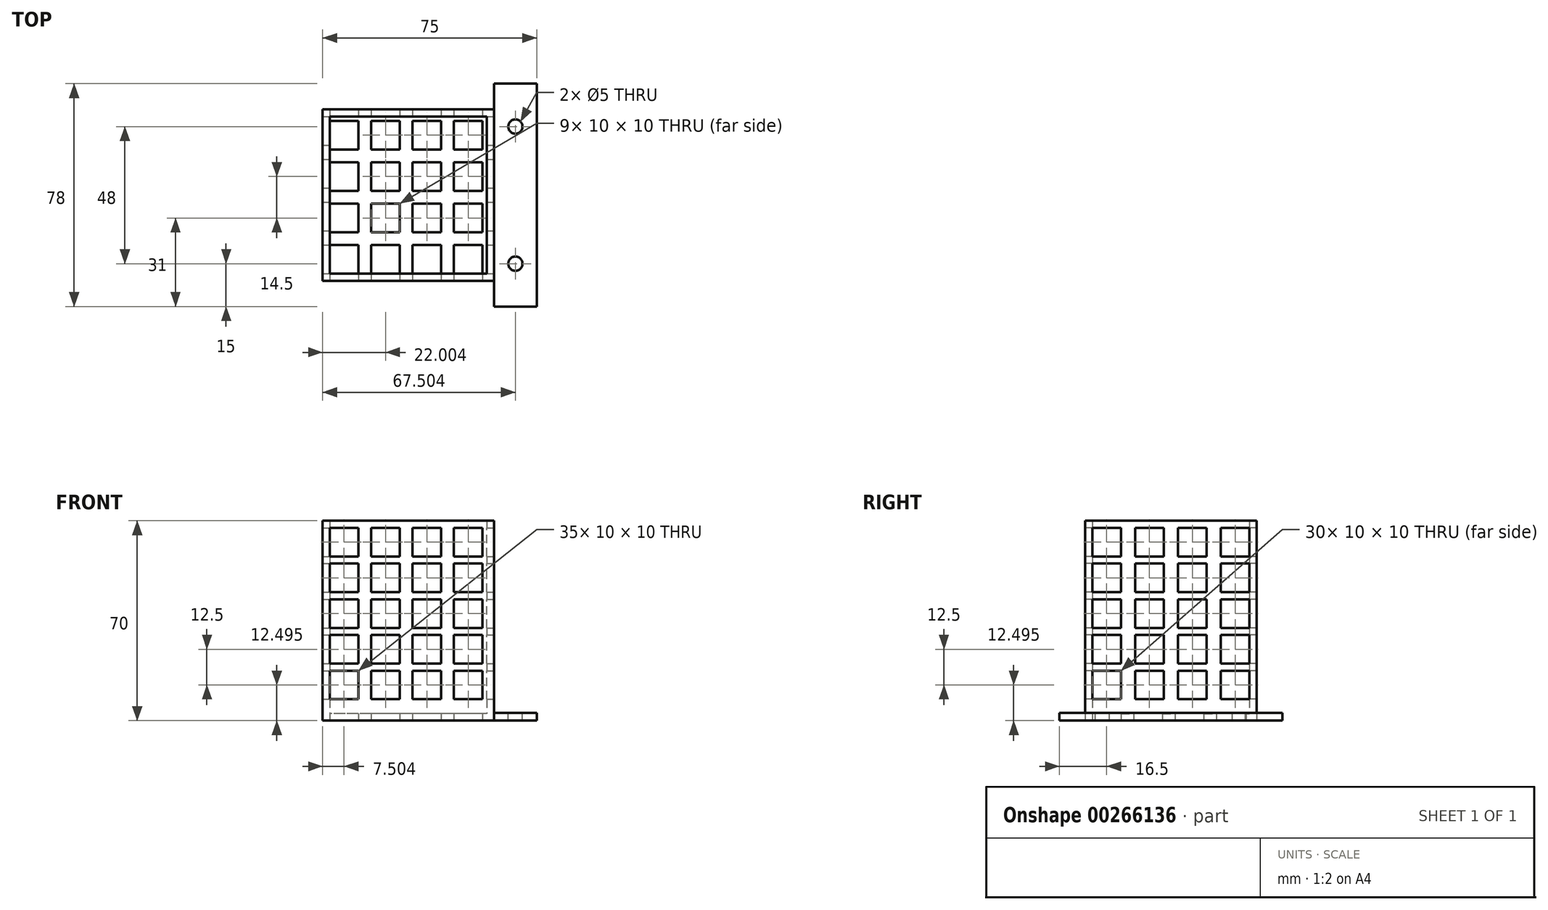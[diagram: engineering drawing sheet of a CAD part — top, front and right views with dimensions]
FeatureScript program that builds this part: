
annotation { "Feature Type Name" : "Feature", "Feature Type Description" : "" }
export const myFeature = defineFeature(function(context is Context, id is Id, definition is map)
    precondition{}
    {
        {
            var Q0;
            Q0=qCreatedBy(makeId("Front.planeOp"),FACE);
            var sketch = newSketch(context, id + "F0", { "sketchPlane" : qUnion([Q0])});
            skLineSegment(sketch, "E0", {"start": v(33.02, 18.38) * mm, "end": v(48.02, 18.38) * mm});
            skLineSegment(sketch, "E1", {"start": v(48.02, 18.38) * mm, "end": v(48.02, 21.13) * mm});
            skLineSegment(sketch, "E2", {"start": v(48.02, 21.13) * mm, "end": v(33.02, 21.13) * mm});
            skLineSegment(sketch, "E3", {"start": v(33.02, 21.13) * mm, "end": v(33.02, 18.38) * mm});
            skSolve(sketch);
        }
        {
            var Q0;
            Q0=qSketchRegion(id+"F0",true);
            extrude(context, id + "F1", {"entities" : qUnion([Q0]), "endBound" : BoundingType.SYMMETRIC, "depth" : 78 * mm});
        }
        {
            var Q0;
            Q0=makeQuery(id+"F1.opExtrude","SWEPT_FACE",FACE,{"disambiguationData":[OSD([sQuery(id+"F0.wireOp",EDGE,"E2")])]});
            var sketch = newSketch(context, id + "F2", { "sketchPlane" : qUnion([Q0])});
            skCircle(sketch, "E4", {"center": v(40.52, -24) * mm, "radius": 2.5 * mm});
            skCircle(sketch, "E5.0.1.0", {"center": v(40.52, 24) * mm, "radius": 2.5 * mm});
            skLineSegment(sketch, "E5.direction1", {"start": v(40.52, -24) * mm, "end": v(64.68, -24) * mm, "construction": true});
            skLineSegment(sketch, "E5.direction2", {"start": v(40.52, -24) * mm, "end": v(40.52, 24) * mm, "construction": true});
            skLineSegment(sketch, "E6.0", {"start": v(33.02, -39) * mm, "end": v(33.02, 39) * mm});
            skLineSegment(sketch, "E7.0", {"start": v(48.02, -39) * mm, "end": v(48.02, 39) * mm});
            skLineSegment(sketch, "E8", {"start": v(33.02, -1.08) * mm, "end": v(48.02, -1.08) * mm, "construction": true});
            skPoint(sketch, "E8.endSnap0", {"position": v(48.02, 0) * mm});
            skPoint(sketch, "E9", {"position": v(40.52, -1.08) * mm});
            skSolve(sketch);
        }
        {
            var Q0;
            Q0=makeQuery(id+"F2.imprint","IMPRINT",FACE,{"disambiguationData":[TD([[makeQuery(id+"F2.imprint","IMPRINT",EDGE,{"derivedFrom":sQuery(id+"F2.wireOp",EDGE,"E5.0.1.0")}),1.0]])]});
            var Q1;
            Q1=makeQuery(id+"F2.imprint","IMPRINT",FACE,{"disambiguationData":[TD([[makeQuery(id+"F2.imprint","IMPRINT",EDGE,{"derivedFrom":sQuery(id+"F2.wireOp",EDGE,"E4")}),1.0]])]});
            extrude(context, id + "F3", {"entities" : qUnion([Q0, Q1]), "operationType" : NewBodyOperationType.REMOVE, "endBound" : BoundingType.THROUGH_ALL, "oppositeDirection" : true, "depth" : 25 * mm});
        }
        {
            var Q0;
            Q0=makeQuery(id+"F1.opExtrude","SWEPT_FACE",FACE,{"disambiguationData":[OSD([sQuery(id+"F0.wireOp",EDGE,"E0")])]});
            var sketch = newSketch(context, id + "F4", { "sketchPlane" : qUnion([Q0])});
            skLineSegment(sketch, "E10", {"start": v(33.02, 30) * mm, "end": v(-26.98, 30) * mm});
            skLineSegment(sketch, "E11", {"start": v(33.02, -30) * mm, "end": v(-26.98, -30) * mm});
            skLineSegment(sketch, "E12", {"start": v(-26.98, 30) * mm, "end": v(-26.98, -30) * mm});
            skSolve(sketch);
        }
        {
            var Q0;
            {var subQ0=sQuery(id+"F4.wireOp",EDGE,"E10");Q0=makeQuery(id+"F4.imprint","IMPRINT",FACE,{"disambiguationData":[TD([[makeQuery(id+"F4.imprint","IMPRINT",EDGE,{"derivedFrom":subQ0}),1.0]])]});}
            extrude(context, id + "F5", {"entities" : qUnion([Q0]), "operationType" : NewBodyOperationType.ADD, "oppositeDirection" : true, "depth" : 70 * mm});
        }
        {
            var Q0;
            Q0=makeQuery(id+"F5.opExtrude","CAP_FACE",FACE,{"disambiguationData":[OSD([sQuery(id+"F0.wireOp",EDGE,"E0"),sQuery(id+"F0.wireOp",EDGE,"E3"),sQuery(id+"F4.wireOp",EDGE,"E10"),sQuery(id+"F4.wireOp",EDGE,"E11"),sQuery(id+"F4.wireOp",EDGE,"XroIyZZh-nZdX-ji37-o0S8-ZtPrHTp5OUbo")])],"isStart":false});
            shell(context, id + "F6", {"entities" : qUnion([Q0]), "thickness" : 2.5 * mm});
        }
        {
            var Q0;
            Q0=makeQuery(id+"F5.opExtrude","SWEPT_FACE",FACE,{"disambiguationData":[OSD([sQuery(id+"F0.wireOp",EDGE,"E0"),sQuery(id+"F0.wireOp",EDGE,"E3")])]});
            var sketch = newSketch(context, id + "F7", { "sketchPlane" : qUnion([Q0])});
            skLineSegment(sketch, "E13.bottom", {"start": v(-27.5, 85.88) * mm, "end": v(-17.5, 85.88) * mm});
            skLineSegment(sketch, "E13.top", {"start": v(-27.5, 75.88) * mm, "end": v(-17.5, 75.88) * mm});
            skLineSegment(sketch, "E13.left", {"start": v(-27.5, 85.88) * mm, "end": v(-27.5, 75.88) * mm});
            skLineSegment(sketch, "E13.right", {"start": v(-17.5, 85.88) * mm, "end": v(-17.5, 75.88) * mm});
            skLineSegment(sketch, "E14.0.1.0", {"start": v(-27.5, 73.38) * mm, "end": v(-17.5, 73.38) * mm});
            skLineSegment(sketch, "E14.0.1.1", {"start": v(-27.5, 73.38) * mm, "end": v(-27.5, 63.38) * mm});
            skLineSegment(sketch, "E14.0.1.2", {"start": v(-27.5, 63.38) * mm, "end": v(-17.5, 63.38) * mm});
            skLineSegment(sketch, "E14.0.1.3", {"start": v(-17.5, 73.38) * mm, "end": v(-17.5, 63.38) * mm});
            skLineSegment(sketch, "E14.0.2.0", {"start": v(-27.5, 60.88) * mm, "end": v(-17.5, 60.88) * mm});
            skLineSegment(sketch, "E14.0.2.1", {"start": v(-27.5, 60.88) * mm, "end": v(-27.5, 50.88) * mm});
            skLineSegment(sketch, "E14.0.2.2", {"start": v(-27.5, 50.88) * mm, "end": v(-17.5, 50.88) * mm});
            skLineSegment(sketch, "E14.0.2.3", {"start": v(-17.5, 60.88) * mm, "end": v(-17.5, 50.88) * mm});
            skLineSegment(sketch, "E14.0.3.0", {"start": v(-27.5, 48.38) * mm, "end": v(-17.5, 48.38) * mm});
            skLineSegment(sketch, "E14.0.3.1", {"start": v(-27.5, 48.38) * mm, "end": v(-27.5, 38.38) * mm});
            skLineSegment(sketch, "E14.0.3.2", {"start": v(-27.5, 38.38) * mm, "end": v(-17.5, 38.38) * mm});
            skLineSegment(sketch, "E14.0.3.3", {"start": v(-17.5, 48.38) * mm, "end": v(-17.5, 38.38) * mm});
            skLineSegment(sketch, "E14.0.4.0", {"start": v(-27.5, 35.88) * mm, "end": v(-17.5, 35.88) * mm});
            skLineSegment(sketch, "E14.0.4.1", {"start": v(-27.5, 35.88) * mm, "end": v(-27.5, 25.88) * mm});
            skLineSegment(sketch, "E14.0.4.2", {"start": v(-27.5, 25.88) * mm, "end": v(-17.5, 25.88) * mm});
            skLineSegment(sketch, "E14.0.4.3", {"start": v(-17.5, 35.88) * mm, "end": v(-17.5, 25.88) * mm});
            skLineSegment(sketch, "E14.1.0.0", {"start": v(-12.5, 85.88) * mm, "end": v(-2.5, 85.88) * mm});
            skLineSegment(sketch, "E14.1.0.1", {"start": v(-12.5, 85.88) * mm, "end": v(-12.5, 75.88) * mm});
            skLineSegment(sketch, "E14.1.0.2", {"start": v(-12.5, 75.88) * mm, "end": v(-2.5, 75.88) * mm});
            skLineSegment(sketch, "E14.1.0.3", {"start": v(-2.5, 85.88) * mm, "end": v(-2.5, 75.88) * mm});
            skLineSegment(sketch, "E14.1.1.0", {"start": v(-12.5, 73.38) * mm, "end": v(-2.5, 73.38) * mm});
            skLineSegment(sketch, "E14.1.1.1", {"start": v(-12.5, 73.38) * mm, "end": v(-12.5, 63.38) * mm});
            skLineSegment(sketch, "E14.1.1.2", {"start": v(-12.5, 63.38) * mm, "end": v(-2.5, 63.38) * mm});
            skLineSegment(sketch, "E14.1.1.3", {"start": v(-2.5, 73.38) * mm, "end": v(-2.5, 63.38) * mm});
            skLineSegment(sketch, "E14.1.2.0", {"start": v(-12.5, 60.88) * mm, "end": v(-2.5, 60.88) * mm});
            skLineSegment(sketch, "E14.1.2.1", {"start": v(-12.5, 60.88) * mm, "end": v(-12.5, 50.88) * mm});
            skLineSegment(sketch, "E14.1.2.2", {"start": v(-12.5, 50.88) * mm, "end": v(-2.5, 50.88) * mm});
            skLineSegment(sketch, "E14.1.2.3", {"start": v(-2.5, 60.88) * mm, "end": v(-2.5, 50.88) * mm});
            skLineSegment(sketch, "E14.1.3.0", {"start": v(-12.5, 48.38) * mm, "end": v(-2.5, 48.38) * mm});
            skLineSegment(sketch, "E14.1.3.1", {"start": v(-12.5, 48.38) * mm, "end": v(-12.5, 38.38) * mm});
            skLineSegment(sketch, "E14.1.3.2", {"start": v(-12.5, 38.38) * mm, "end": v(-2.5, 38.38) * mm});
            skLineSegment(sketch, "E14.1.3.3", {"start": v(-2.5, 48.38) * mm, "end": v(-2.5, 38.38) * mm});
            skLineSegment(sketch, "E14.1.4.0", {"start": v(-12.5, 35.88) * mm, "end": v(-2.5, 35.88) * mm});
            skLineSegment(sketch, "E14.1.4.1", {"start": v(-12.5, 35.88) * mm, "end": v(-12.5, 25.88) * mm});
            skLineSegment(sketch, "E14.1.4.2", {"start": v(-12.5, 25.88) * mm, "end": v(-2.5, 25.88) * mm});
            skLineSegment(sketch, "E14.1.4.3", {"start": v(-2.5, 35.88) * mm, "end": v(-2.5, 25.88) * mm});
            skLineSegment(sketch, "E14.2.0.0", {"start": v(2.5, 85.88) * mm, "end": v(12.5, 85.88) * mm});
            skLineSegment(sketch, "E14.2.0.1", {"start": v(2.5, 85.88) * mm, "end": v(2.5, 75.88) * mm});
            skLineSegment(sketch, "E14.2.0.2", {"start": v(2.5, 75.88) * mm, "end": v(12.5, 75.88) * mm});
            skLineSegment(sketch, "E14.2.0.3", {"start": v(12.5, 85.88) * mm, "end": v(12.5, 75.88) * mm});
            skLineSegment(sketch, "E14.2.1.0", {"start": v(2.5, 73.38) * mm, "end": v(12.5, 73.38) * mm});
            skLineSegment(sketch, "E14.2.1.1", {"start": v(2.5, 73.38) * mm, "end": v(2.5, 63.38) * mm});
            skLineSegment(sketch, "E14.2.1.2", {"start": v(2.5, 63.38) * mm, "end": v(12.5, 63.38) * mm});
            skLineSegment(sketch, "E14.2.1.3", {"start": v(12.5, 73.38) * mm, "end": v(12.5, 63.38) * mm});
            skLineSegment(sketch, "E14.2.2.0", {"start": v(2.5, 60.88) * mm, "end": v(12.5, 60.88) * mm});
            skLineSegment(sketch, "E14.2.2.1", {"start": v(2.5, 60.88) * mm, "end": v(2.5, 50.88) * mm});
            skLineSegment(sketch, "E14.2.2.2", {"start": v(2.5, 50.88) * mm, "end": v(12.5, 50.88) * mm});
            skLineSegment(sketch, "E14.2.2.3", {"start": v(12.5, 60.88) * mm, "end": v(12.5, 50.88) * mm});
            skLineSegment(sketch, "E14.2.3.0", {"start": v(2.5, 48.38) * mm, "end": v(12.5, 48.38) * mm});
            skLineSegment(sketch, "E14.2.3.1", {"start": v(2.5, 48.38) * mm, "end": v(2.5, 38.38) * mm});
            skLineSegment(sketch, "E14.2.3.2", {"start": v(2.5, 38.38) * mm, "end": v(12.5, 38.38) * mm});
            skLineSegment(sketch, "E14.2.3.3", {"start": v(12.5, 48.38) * mm, "end": v(12.5, 38.38) * mm});
            skLineSegment(sketch, "E14.2.4.0", {"start": v(2.5, 35.88) * mm, "end": v(12.5, 35.88) * mm});
            skLineSegment(sketch, "E14.2.4.1", {"start": v(2.5, 35.88) * mm, "end": v(2.5, 25.88) * mm});
            skLineSegment(sketch, "E14.2.4.2", {"start": v(2.5, 25.88) * mm, "end": v(12.5, 25.88) * mm});
            skLineSegment(sketch, "E14.2.4.3", {"start": v(12.5, 35.88) * mm, "end": v(12.5, 25.88) * mm});
            skLineSegment(sketch, "E14.3.0.0", {"start": v(17.5, 85.88) * mm, "end": v(27.5, 85.88) * mm});
            skLineSegment(sketch, "E14.3.0.1", {"start": v(17.5, 85.88) * mm, "end": v(17.5, 75.88) * mm});
            skLineSegment(sketch, "E14.3.0.2", {"start": v(17.5, 75.88) * mm, "end": v(27.5, 75.88) * mm});
            skLineSegment(sketch, "E14.3.0.3", {"start": v(27.5, 85.88) * mm, "end": v(27.5, 75.88) * mm});
            skLineSegment(sketch, "E14.3.1.0", {"start": v(17.5, 73.38) * mm, "end": v(27.5, 73.38) * mm});
            skLineSegment(sketch, "E14.3.1.1", {"start": v(17.5, 73.38) * mm, "end": v(17.5, 63.38) * mm});
            skLineSegment(sketch, "E14.3.1.2", {"start": v(17.5, 63.38) * mm, "end": v(27.5, 63.38) * mm});
            skLineSegment(sketch, "E14.3.1.3", {"start": v(27.5, 73.38) * mm, "end": v(27.5, 63.38) * mm});
            skLineSegment(sketch, "E14.3.2.0", {"start": v(17.5, 60.88) * mm, "end": v(27.5, 60.88) * mm});
            skLineSegment(sketch, "E14.3.2.1", {"start": v(17.5, 60.88) * mm, "end": v(17.5, 50.88) * mm});
            skLineSegment(sketch, "E14.3.2.2", {"start": v(17.5, 50.88) * mm, "end": v(27.5, 50.88) * mm});
            skLineSegment(sketch, "E14.3.2.3", {"start": v(27.5, 60.88) * mm, "end": v(27.5, 50.88) * mm});
            skLineSegment(sketch, "E14.3.3.0", {"start": v(17.5, 48.38) * mm, "end": v(27.5, 48.38) * mm});
            skLineSegment(sketch, "E14.3.3.1", {"start": v(17.5, 48.38) * mm, "end": v(17.5, 38.38) * mm});
            skLineSegment(sketch, "E14.3.3.2", {"start": v(17.5, 38.38) * mm, "end": v(27.5, 38.38) * mm});
            skLineSegment(sketch, "E14.3.3.3", {"start": v(27.5, 48.38) * mm, "end": v(27.5, 38.38) * mm});
            skLineSegment(sketch, "E14.3.4.0", {"start": v(17.5, 35.88) * mm, "end": v(27.5, 35.88) * mm});
            skLineSegment(sketch, "E14.3.4.1", {"start": v(17.5, 35.88) * mm, "end": v(17.5, 25.88) * mm});
            skLineSegment(sketch, "E14.3.4.2", {"start": v(17.5, 25.88) * mm, "end": v(27.5, 25.88) * mm});
            skLineSegment(sketch, "E14.3.4.3", {"start": v(27.5, 35.88) * mm, "end": v(27.5, 25.88) * mm});
            skLineSegment(sketch, "E14.direction1", {"start": v(-27.5, 85.88) * mm, "end": v(-12.5, 85.88) * mm, "construction": true});
            skLineSegment(sketch, "E14.direction2", {"start": v(-27.5, 85.88) * mm, "end": v(-27.5, 73.38) * mm, "construction": true});
            skSolve(sketch);
        }
        {
            var Q0;
            Q0=makeQuery(id+"F7.imprint","IMPRINT",FACE,{"disambiguationData":[TD([[makeQuery(id+"F7.imprint","IMPRINT",EDGE,{"derivedFrom":sQuery(id+"F7.wireOp",EDGE,"E13.bottom")}),-1.0]])]});
            var Q1;
            Q1=makeQuery(id+"F7.imprint","IMPRINT",FACE,{"disambiguationData":[TD([[makeQuery(id+"F7.imprint","IMPRINT",EDGE,{"derivedFrom":sQuery(id+"F7.wireOp",EDGE,"E14.1.0.0")}),-1.0]])]});
            var Q2;
            Q2=makeQuery(id+"F7.imprint","IMPRINT",FACE,{"disambiguationData":[TD([[makeQuery(id+"F7.imprint","IMPRINT",EDGE,{"derivedFrom":sQuery(id+"F7.wireOp",EDGE,"E14.2.0.0")}),-1.0]])]});
            var Q3;
            Q3=makeQuery(id+"F7.imprint","IMPRINT",FACE,{"disambiguationData":[TD([[makeQuery(id+"F7.imprint","IMPRINT",EDGE,{"derivedFrom":sQuery(id+"F7.wireOp",EDGE,"E14.3.0.0")}),-1.0]])]});
            var Q4;
            Q4=makeQuery(id+"F7.imprint","IMPRINT",FACE,{"disambiguationData":[TD([[makeQuery(id+"F7.imprint","IMPRINT",EDGE,{"derivedFrom":sQuery(id+"F7.wireOp",EDGE,"E14.3.1.0")}),-1.0]])]});
            var Q5;
            Q5=makeQuery(id+"F7.imprint","IMPRINT",FACE,{"disambiguationData":[TD([[makeQuery(id+"F7.imprint","IMPRINT",EDGE,{"derivedFrom":sQuery(id+"F7.wireOp",EDGE,"E14.0.1.0")}),-1.0]])]});
            var Q6;
            Q6=makeQuery(id+"F7.imprint","IMPRINT",FACE,{"disambiguationData":[TD([[makeQuery(id+"F7.imprint","IMPRINT",EDGE,{"derivedFrom":sQuery(id+"F7.wireOp",EDGE,"E14.1.1.0")}),-1.0]])]});
            var Q7;
            Q7=makeQuery(id+"F7.imprint","IMPRINT",FACE,{"disambiguationData":[TD([[makeQuery(id+"F7.imprint","IMPRINT",EDGE,{"derivedFrom":sQuery(id+"F7.wireOp",EDGE,"E14.2.1.0")}),-1.0]])]});
            var Q8;
            Q8=makeQuery(id+"F7.imprint","IMPRINT",FACE,{"disambiguationData":[TD([[makeQuery(id+"F7.imprint","IMPRINT",EDGE,{"derivedFrom":sQuery(id+"F7.wireOp",EDGE,"E14.2.2.0")}),-1.0]])]});
            var Q9;
            Q9=makeQuery(id+"F7.imprint","IMPRINT",FACE,{"disambiguationData":[TD([[makeQuery(id+"F7.imprint","IMPRINT",EDGE,{"derivedFrom":sQuery(id+"F7.wireOp",EDGE,"E14.3.2.0")}),-1.0]])]});
            var Q10;
            Q10=makeQuery(id+"F7.imprint","IMPRINT",FACE,{"disambiguationData":[TD([[makeQuery(id+"F7.imprint","IMPRINT",EDGE,{"derivedFrom":sQuery(id+"F7.wireOp",EDGE,"E14.1.2.0")}),-1.0]])]});
            var Q11;
            Q11=makeQuery(id+"F7.imprint","IMPRINT",FACE,{"disambiguationData":[TD([[makeQuery(id+"F7.imprint","IMPRINT",EDGE,{"derivedFrom":sQuery(id+"F7.wireOp",EDGE,"E14.0.2.0")}),-1.0]])]});
            var Q12;
            Q12=makeQuery(id+"F7.imprint","IMPRINT",FACE,{"disambiguationData":[TD([[makeQuery(id+"F7.imprint","IMPRINT",EDGE,{"derivedFrom":sQuery(id+"F7.wireOp",EDGE,"E14.0.3.0")}),-1.0]])]});
            var Q13;
            Q13=makeQuery(id+"F7.imprint","IMPRINT",FACE,{"disambiguationData":[TD([[makeQuery(id+"F7.imprint","IMPRINT",EDGE,{"derivedFrom":sQuery(id+"F7.wireOp",EDGE,"E14.1.3.0")}),-1.0]])]});
            var Q14;
            Q14=makeQuery(id+"F7.imprint","IMPRINT",FACE,{"disambiguationData":[TD([[makeQuery(id+"F7.imprint","IMPRINT",EDGE,{"derivedFrom":sQuery(id+"F7.wireOp",EDGE,"E14.1.4.0")}),-1.0]])]});
            var Q15;
            Q15=makeQuery(id+"F7.imprint","IMPRINT",FACE,{"disambiguationData":[TD([[makeQuery(id+"F7.imprint","IMPRINT",EDGE,{"derivedFrom":sQuery(id+"F7.wireOp",EDGE,"E14.0.4.0")}),-1.0]])]});
            var Q16;
            Q16=makeQuery(id+"F7.imprint","IMPRINT",FACE,{"disambiguationData":[TD([[makeQuery(id+"F7.imprint","IMPRINT",EDGE,{"derivedFrom":sQuery(id+"F7.wireOp",EDGE,"E14.2.3.0")}),-1.0]])]});
            var Q17;
            Q17=makeQuery(id+"F7.imprint","IMPRINT",FACE,{"disambiguationData":[TD([[makeQuery(id+"F7.imprint","IMPRINT",EDGE,{"derivedFrom":sQuery(id+"F7.wireOp",EDGE,"E14.2.4.0")}),-1.0]])]});
            var Q18;
            Q18=makeQuery(id+"F7.imprint","IMPRINT",FACE,{"disambiguationData":[TD([[makeQuery(id+"F7.imprint","IMPRINT",EDGE,{"derivedFrom":sQuery(id+"F7.wireOp",EDGE,"E14.3.4.0")}),-1.0]])]});
            var Q19;
            Q19=makeQuery(id+"F7.imprint","IMPRINT",FACE,{"disambiguationData":[TD([[makeQuery(id+"F7.imprint","IMPRINT",EDGE,{"derivedFrom":sQuery(id+"F7.wireOp",EDGE,"E14.3.3.0")}),-1.0]])]});
            var Q20;
            Q20=makeQuery(id+"F6.opShell","OFFSET_FACE",FACE,{"disambiguationData":[OSD([sQuery(id+"F0.wireOp",EDGE,"E0"),sQuery(id+"F0.wireOp",EDGE,"E3")])]});
            extrude(context, id + "F8", {"entities" : qUnion([Q0, Q1, Q2, Q3, Q4, Q5, Q6, Q7, Q8, Q9, Q10, Q11, Q12, Q13, Q14, Q15, Q16, Q17, Q18, Q19]), "operationType" : NewBodyOperationType.REMOVE, "endBound" : BoundingType.THROUGH_ALL, "oppositeDirection" : true, "endBoundEntityFace" : qUnion([Q20]), "depth" : 25 * mm});
        }
        {
            var Q0;
            Q0=makeQuery(id+"F5.opExtrude","SWEPT_FACE",FACE,{"disambiguationData":[OSD([sQuery(id+"F4.wireOp",EDGE,"E10")])]});
            var sketch = newSketch(context, id + "F9", { "sketchPlane" : qUnion([Q0])});
            skLineSegment(sketch, "E15.bottom", {"start": v(-24.48, 85.88) * mm, "end": v(-14.48, 85.88) * mm});
            skLineSegment(sketch, "E15.top", {"start": v(-24.48, 75.88) * mm, "end": v(-14.48, 75.88) * mm});
            skLineSegment(sketch, "E15.left", {"start": v(-24.48, 85.88) * mm, "end": v(-24.48, 75.88) * mm});
            skLineSegment(sketch, "E15.right", {"start": v(-14.48, 85.88) * mm, "end": v(-14.48, 75.88) * mm});
            skLineSegment(sketch, "E16.0.1.0", {"start": v(-24.48, 73.38) * mm, "end": v(-14.48, 73.38) * mm});
            skLineSegment(sketch, "E16.0.1.1", {"start": v(-24.48, 73.38) * mm, "end": v(-24.48, 63.38) * mm});
            skLineSegment(sketch, "E16.0.1.2", {"start": v(-14.48, 73.38) * mm, "end": v(-14.48, 63.38) * mm});
            skLineSegment(sketch, "E16.0.1.3", {"start": v(-24.48, 63.38) * mm, "end": v(-14.48, 63.38) * mm});
            skLineSegment(sketch, "E16.0.2.0", {"start": v(-24.48, 60.88) * mm, "end": v(-14.48, 60.88) * mm});
            skLineSegment(sketch, "E16.0.2.1", {"start": v(-24.48, 60.88) * mm, "end": v(-24.48, 50.88) * mm});
            skLineSegment(sketch, "E16.0.2.2", {"start": v(-14.48, 60.88) * mm, "end": v(-14.48, 50.88) * mm});
            skLineSegment(sketch, "E16.0.2.3", {"start": v(-24.48, 50.88) * mm, "end": v(-14.48, 50.88) * mm});
            skLineSegment(sketch, "E16.0.3.0", {"start": v(-24.48, 48.38) * mm, "end": v(-14.48, 48.38) * mm});
            skLineSegment(sketch, "E16.0.3.1", {"start": v(-24.48, 48.38) * mm, "end": v(-24.48, 38.38) * mm});
            skLineSegment(sketch, "E16.0.3.2", {"start": v(-14.48, 48.38) * mm, "end": v(-14.48, 38.38) * mm});
            skLineSegment(sketch, "E16.0.3.3", {"start": v(-24.48, 38.38) * mm, "end": v(-14.48, 38.38) * mm});
            skLineSegment(sketch, "E16.0.4.0", {"start": v(-24.48, 35.88) * mm, "end": v(-14.48, 35.88) * mm});
            skLineSegment(sketch, "E16.0.4.1", {"start": v(-24.48, 35.88) * mm, "end": v(-24.48, 25.88) * mm});
            skLineSegment(sketch, "E16.0.4.2", {"start": v(-14.48, 35.88) * mm, "end": v(-14.48, 25.88) * mm});
            skLineSegment(sketch, "E16.0.4.3", {"start": v(-24.48, 25.88) * mm, "end": v(-14.48, 25.88) * mm});
            skLineSegment(sketch, "E16.1.0.0", {"start": v(-9.98, 85.88) * mm, "end": v(0.02, 85.88) * mm});
            skLineSegment(sketch, "E16.1.0.1", {"start": v(-9.98, 85.88) * mm, "end": v(-9.98, 75.88) * mm});
            skLineSegment(sketch, "E16.1.0.2", {"start": v(0.02, 85.88) * mm, "end": v(0.02, 75.88) * mm});
            skLineSegment(sketch, "E16.1.0.3", {"start": v(-9.98, 75.88) * mm, "end": v(0.02, 75.88) * mm});
            skLineSegment(sketch, "E16.1.1.0", {"start": v(-9.98, 73.38) * mm, "end": v(0.02, 73.38) * mm});
            skLineSegment(sketch, "E16.1.1.1", {"start": v(-9.98, 73.38) * mm, "end": v(-9.98, 63.38) * mm});
            skLineSegment(sketch, "E16.1.1.2", {"start": v(0.02, 73.38) * mm, "end": v(0.02, 63.38) * mm});
            skLineSegment(sketch, "E16.1.1.3", {"start": v(-9.98, 63.38) * mm, "end": v(0.02, 63.38) * mm});
            skLineSegment(sketch, "E16.1.2.0", {"start": v(-9.98, 60.88) * mm, "end": v(0.02, 60.88) * mm});
            skLineSegment(sketch, "E16.1.2.1", {"start": v(-9.98, 60.88) * mm, "end": v(-9.98, 50.88) * mm});
            skLineSegment(sketch, "E16.1.2.2", {"start": v(0.02, 60.88) * mm, "end": v(0.02, 50.88) * mm});
            skLineSegment(sketch, "E16.1.2.3", {"start": v(-9.98, 50.88) * mm, "end": v(0.02, 50.88) * mm});
            skLineSegment(sketch, "E16.1.3.0", {"start": v(-9.98, 48.38) * mm, "end": v(0.02, 48.38) * mm});
            skLineSegment(sketch, "E16.1.3.1", {"start": v(-9.98, 48.38) * mm, "end": v(-9.98, 38.38) * mm});
            skLineSegment(sketch, "E16.1.3.2", {"start": v(0.02, 48.38) * mm, "end": v(0.02, 38.38) * mm});
            skLineSegment(sketch, "E16.1.3.3", {"start": v(-9.98, 38.38) * mm, "end": v(0.02, 38.38) * mm});
            skLineSegment(sketch, "E16.1.4.0", {"start": v(-9.98, 35.88) * mm, "end": v(0.02, 35.88) * mm});
            skLineSegment(sketch, "E16.1.4.1", {"start": v(-9.98, 35.88) * mm, "end": v(-9.98, 25.88) * mm});
            skLineSegment(sketch, "E16.1.4.2", {"start": v(0.02, 35.88) * mm, "end": v(0.02, 25.88) * mm});
            skLineSegment(sketch, "E16.1.4.3", {"start": v(-9.98, 25.88) * mm, "end": v(0.02, 25.88) * mm});
            skLineSegment(sketch, "E16.direction1", {"start": v(-24.48, 85.88) * mm, "end": v(-9.98, 85.88) * mm, "construction": true});
            skLineSegment(sketch, "E16.direction2", {"start": v(-24.48, 85.88) * mm, "end": v(-24.48, 73.38) * mm, "construction": true});
            skLineSegment(sketch, "E17.0.2.0", {"start": v(4.52, 85.88) * mm, "end": v(14.52, 85.88) * mm});
            skLineSegment(sketch, "E17.3.2.0", {"start": v(4.52, 85.88) * mm, "end": v(4.52, 75.88) * mm});
            skLineSegment(sketch, "E17.6.2.0", {"start": v(14.52, 85.88) * mm, "end": v(14.52, 75.88) * mm});
            skLineSegment(sketch, "E17.9.2.0", {"start": v(4.52, 75.88) * mm, "end": v(14.52, 75.88) * mm});
            skLineSegment(sketch, "E17.0.2.1", {"start": v(4.52, 73.38) * mm, "end": v(14.52, 73.38) * mm});
            skLineSegment(sketch, "E17.3.2.1", {"start": v(4.52, 73.38) * mm, "end": v(4.52, 63.38) * mm});
            skLineSegment(sketch, "E17.6.2.1", {"start": v(14.52, 73.38) * mm, "end": v(14.52, 63.38) * mm});
            skLineSegment(sketch, "E17.9.2.1", {"start": v(4.52, 63.38) * mm, "end": v(14.52, 63.38) * mm});
            skLineSegment(sketch, "E17.0.2.2", {"start": v(4.52, 60.88) * mm, "end": v(14.52, 60.88) * mm});
            skLineSegment(sketch, "E17.3.2.2", {"start": v(4.52, 60.88) * mm, "end": v(4.52, 50.88) * mm});
            skLineSegment(sketch, "E17.6.2.2", {"start": v(14.52, 60.88) * mm, "end": v(14.52, 50.88) * mm});
            skLineSegment(sketch, "E17.9.2.2", {"start": v(4.52, 50.88) * mm, "end": v(14.52, 50.88) * mm});
            skLineSegment(sketch, "E17.0.2.3", {"start": v(4.52, 48.38) * mm, "end": v(14.52, 48.38) * mm});
            skLineSegment(sketch, "E17.3.2.3", {"start": v(4.52, 48.38) * mm, "end": v(4.52, 38.38) * mm});
            skLineSegment(sketch, "E17.6.2.3", {"start": v(14.52, 48.38) * mm, "end": v(14.52, 38.38) * mm});
            skLineSegment(sketch, "E17.9.2.3", {"start": v(4.52, 38.38) * mm, "end": v(14.52, 38.38) * mm});
            skLineSegment(sketch, "E17.0.2.4", {"start": v(4.52, 35.88) * mm, "end": v(14.52, 35.88) * mm});
            skLineSegment(sketch, "E17.3.2.4", {"start": v(4.52, 35.88) * mm, "end": v(4.52, 25.88) * mm});
            skLineSegment(sketch, "E17.6.2.4", {"start": v(14.52, 35.88) * mm, "end": v(14.52, 25.88) * mm});
            skLineSegment(sketch, "E17.9.2.4", {"start": v(4.52, 25.88) * mm, "end": v(14.52, 25.88) * mm});
            skLineSegment(sketch, "E17.0.3.0", {"start": v(19.02, 85.88) * mm, "end": v(29.02, 85.88) * mm});
            skLineSegment(sketch, "E17.3.3.0", {"start": v(19.02, 85.88) * mm, "end": v(19.02, 75.88) * mm});
            skLineSegment(sketch, "E17.6.3.0", {"start": v(29.02, 85.88) * mm, "end": v(29.02, 75.88) * mm});
            skLineSegment(sketch, "E17.9.3.0", {"start": v(19.02, 75.88) * mm, "end": v(29.02, 75.88) * mm});
            skLineSegment(sketch, "E17.0.3.1", {"start": v(19.02, 73.38) * mm, "end": v(29.02, 73.38) * mm});
            skLineSegment(sketch, "E17.3.3.1", {"start": v(19.02, 73.38) * mm, "end": v(19.02, 63.38) * mm});
            skLineSegment(sketch, "E17.6.3.1", {"start": v(29.02, 73.38) * mm, "end": v(29.02, 63.38) * mm});
            skLineSegment(sketch, "E17.9.3.1", {"start": v(19.02, 63.38) * mm, "end": v(29.02, 63.38) * mm});
            skLineSegment(sketch, "E17.0.3.2", {"start": v(19.02, 60.88) * mm, "end": v(29.02, 60.88) * mm});
            skLineSegment(sketch, "E17.3.3.2", {"start": v(19.02, 60.88) * mm, "end": v(19.02, 50.88) * mm});
            skLineSegment(sketch, "E17.6.3.2", {"start": v(29.02, 60.88) * mm, "end": v(29.02, 50.88) * mm});
            skLineSegment(sketch, "E17.9.3.2", {"start": v(19.02, 50.88) * mm, "end": v(29.02, 50.88) * mm});
            skLineSegment(sketch, "E17.0.3.3", {"start": v(19.02, 48.38) * mm, "end": v(29.02, 48.38) * mm});
            skLineSegment(sketch, "E17.3.3.3", {"start": v(19.02, 48.38) * mm, "end": v(19.02, 38.38) * mm});
            skLineSegment(sketch, "E17.6.3.3", {"start": v(29.02, 48.38) * mm, "end": v(29.02, 38.38) * mm});
            skLineSegment(sketch, "E17.9.3.3", {"start": v(19.02, 38.38) * mm, "end": v(29.02, 38.38) * mm});
            skLineSegment(sketch, "E17.0.3.4", {"start": v(19.02, 35.88) * mm, "end": v(29.02, 35.88) * mm});
            skLineSegment(sketch, "E17.3.3.4", {"start": v(19.02, 35.88) * mm, "end": v(19.02, 25.88) * mm});
            skLineSegment(sketch, "E17.6.3.4", {"start": v(29.02, 35.88) * mm, "end": v(29.02, 25.88) * mm});
            skLineSegment(sketch, "E17.9.3.4", {"start": v(19.02, 25.88) * mm, "end": v(29.02, 25.88) * mm});
            skSolve(sketch);
        }
        {
            var Q0;
            Q0=makeQuery(id+"F9.imprint","IMPRINT",FACE,{"disambiguationData":[TD([[makeQuery(id+"F9.imprint","IMPRINT",EDGE,{"derivedFrom":sQuery(id+"F9.wireOp",EDGE,"E15.bottom")}),-1.0]])]});
            var Q1;
            Q1=makeQuery(id+"F9.imprint","IMPRINT",FACE,{"disambiguationData":[TD([[makeQuery(id+"F9.imprint","IMPRINT",EDGE,{"derivedFrom":sQuery(id+"F9.wireOp",EDGE,"E16.1.0.0")}),-1.0]])]});
            var Q2;
            Q2=makeQuery(id+"F9.imprint","IMPRINT",FACE,{"disambiguationData":[TD([[makeQuery(id+"F9.imprint","IMPRINT",EDGE,{"derivedFrom":sQuery(id+"F9.wireOp",EDGE,"E16.1.1.0")}),-1.0]])]});
            var Q3;
            Q3=makeQuery(id+"F9.imprint","IMPRINT",FACE,{"disambiguationData":[TD([[makeQuery(id+"F9.imprint","IMPRINT",EDGE,{"derivedFrom":sQuery(id+"F9.wireOp",EDGE,"E16.0.1.0")}),-1.0]])]});
            var Q4;
            Q4=makeQuery(id+"F9.imprint","IMPRINT",FACE,{"disambiguationData":[TD([[makeQuery(id+"F9.imprint","IMPRINT",EDGE,{"derivedFrom":sQuery(id+"F9.wireOp",EDGE,"E16.1.2.0")}),-1.0]])]});
            var Q5;
            Q5=makeQuery(id+"F9.imprint","IMPRINT",FACE,{"disambiguationData":[TD([[makeQuery(id+"F9.imprint","IMPRINT",EDGE,{"derivedFrom":sQuery(id+"F9.wireOp",EDGE,"E16.0.2.0")}),-1.0]])]});
            var Q6;
            Q6=makeQuery(id+"F9.imprint","IMPRINT",FACE,{"disambiguationData":[TD([[makeQuery(id+"F9.imprint","IMPRINT",EDGE,{"derivedFrom":sQuery(id+"F9.wireOp",EDGE,"E16.0.3.0")}),-1.0]])]});
            var Q7;
            Q7=makeQuery(id+"F9.imprint","IMPRINT",FACE,{"disambiguationData":[TD([[makeQuery(id+"F9.imprint","IMPRINT",EDGE,{"derivedFrom":sQuery(id+"F9.wireOp",EDGE,"E16.1.3.0")}),-1.0]])]});
            var Q8;
            Q8=makeQuery(id+"F9.imprint","IMPRINT",FACE,{"disambiguationData":[TD([[makeQuery(id+"F9.imprint","IMPRINT",EDGE,{"derivedFrom":sQuery(id+"F9.wireOp",EDGE,"E16.1.4.0")}),-1.0]])]});
            var Q9;
            Q9=makeQuery(id+"F9.imprint","IMPRINT",FACE,{"disambiguationData":[TD([[makeQuery(id+"F9.imprint","IMPRINT",EDGE,{"derivedFrom":sQuery(id+"F9.wireOp",EDGE,"E16.0.4.0")}),-1.0]])]});
            var Q10;
            Q10=makeQuery(id+"F9.imprint","IMPRINT",FACE,{"disambiguationData":[TD([[makeQuery(id+"F9.imprint","IMPRINT",EDGE,{"derivedFrom":sQuery(id+"F9.wireOp",EDGE,"adfbc09c-be89-4648-bd99-6bff8c9d6e1d.1.0.0")}),-1.0]])]});
            var Q11;
            Q11=makeQuery(id+"F9.imprint","IMPRINT",FACE,{"disambiguationData":[TD([[makeQuery(id+"F9.imprint","IMPRINT",EDGE,{"derivedFrom":sQuery(id+"F9.wireOp",EDGE,"adfbc09c-be89-4648-bd99-6bff8c9d6e1d.2.0.0")}),-1.0]])]});
            var Q12;
            Q12=makeQuery(id+"F9.imprint","IMPRINT",FACE,{"disambiguationData":[TD([[makeQuery(id+"F9.imprint","IMPRINT",EDGE,{"derivedFrom":sQuery(id+"F9.wireOp",EDGE,"E17.0.2.0")}),-1.0]])]});
            var Q13;
            Q13=makeQuery(id+"F9.imprint","IMPRINT",FACE,{"disambiguationData":[TD([[makeQuery(id+"F9.imprint","IMPRINT",EDGE,{"derivedFrom":sQuery(id+"F9.wireOp",EDGE,"E17.0.3.0")}),-1.0]])]});
            var Q14;
            Q14=makeQuery(id+"F9.imprint","IMPRINT",FACE,{"disambiguationData":[TD([[makeQuery(id+"F9.imprint","IMPRINT",EDGE,{"derivedFrom":sQuery(id+"F9.wireOp",EDGE,"E17.0.3.1")}),-1.0]])]});
            var Q15;
            Q15=makeQuery(id+"F9.imprint","IMPRINT",FACE,{"disambiguationData":[TD([[makeQuery(id+"F9.imprint","IMPRINT",EDGE,{"derivedFrom":sQuery(id+"F9.wireOp",EDGE,"E17.0.2.1")}),-1.0]])]});
            var Q16;
            Q16=makeQuery(id+"F9.imprint","IMPRINT",FACE,{"disambiguationData":[TD([[makeQuery(id+"F9.imprint","IMPRINT",EDGE,{"derivedFrom":sQuery(id+"F9.wireOp",EDGE,"E17.0.2.2")}),-1.0]])]});
            var Q17;
            Q17=makeQuery(id+"F9.imprint","IMPRINT",FACE,{"disambiguationData":[TD([[makeQuery(id+"F9.imprint","IMPRINT",EDGE,{"derivedFrom":sQuery(id+"F9.wireOp",EDGE,"E17.0.3.2")}),-1.0]])]});
            var Q18;
            Q18=makeQuery(id+"F9.imprint","IMPRINT",FACE,{"disambiguationData":[TD([[makeQuery(id+"F9.imprint","IMPRINT",EDGE,{"derivedFrom":sQuery(id+"F9.wireOp",EDGE,"E17.0.2.3")}),-1.0]])]});
            var Q19;
            Q19=makeQuery(id+"F9.imprint","IMPRINT",FACE,{"disambiguationData":[TD([[makeQuery(id+"F9.imprint","IMPRINT",EDGE,{"derivedFrom":sQuery(id+"F9.wireOp",EDGE,"E17.0.3.3")}),-1.0]])]});
            var Q20;
            Q20=makeQuery(id+"F9.imprint","IMPRINT",FACE,{"disambiguationData":[TD([[makeQuery(id+"F9.imprint","IMPRINT",EDGE,{"derivedFrom":sQuery(id+"F9.wireOp",EDGE,"E17.0.3.4")}),-1.0]])]});
            var Q21;
            Q21=makeQuery(id+"F9.imprint","IMPRINT",FACE,{"disambiguationData":[TD([[makeQuery(id+"F9.imprint","IMPRINT",EDGE,{"derivedFrom":sQuery(id+"F9.wireOp",EDGE,"E17.0.2.4")}),-1.0]])]});
            extrude(context, id + "F10", {"entities" : qUnion([Q0, Q1, Q2, Q3, Q4, Q5, Q6, Q7, Q8, Q9, Q10, Q11, Q12, Q13, Q14, Q15, Q16, Q17, Q18, Q19, Q20, Q21]), "operationType" : NewBodyOperationType.REMOVE, "endBound" : BoundingType.THROUGH_ALL, "oppositeDirection" : true, "depth" : 25 * mm});
        }
        {
            var Q0;
            {var subQ0=sQuery(id+"F0.wireOp",EDGE,"E0");Q0=makeQuery(id+"F5.boolean.opBoolean","MERGE",FACE,{"derivedFrom":[makeQuery(id+"F1.opExtrude","SWEPT_FACE",FACE,{"disambiguationData":[OSD([subQ0])]}),makeQuery(id+"F5.opExtrude","CAP_FACE",FACE,{"disambiguationData":[OSD([subQ0,sQuery(id+"F0.wireOp",EDGE,"E3"),sQuery(id+"F4.wireOp",EDGE,"E10"),sQuery(id+"F4.wireOp",EDGE,"E11"),sQuery(id+"F4.wireOp",EDGE,"E12")])],"isStart":true})]});}
            var sketch = newSketch(context, id + "F11", { "sketchPlane" : qUnion([Q0])});
            skLineSegment(sketch, "E18.bottom", {"start": v(-24.48, 27.5) * mm, "end": v(-14.48, 27.5) * mm});
            skLineSegment(sketch, "E18.top", {"start": v(-24.48, 17.5) * mm, "end": v(-14.48, 17.5) * mm});
            skLineSegment(sketch, "E18.left", {"start": v(-24.48, 27.5) * mm, "end": v(-24.48, 17.5) * mm});
            skLineSegment(sketch, "E18.right", {"start": v(-14.48, 27.5) * mm, "end": v(-14.48, 17.5) * mm});
            skLineSegment(sketch, "E19.0.1.0", {"start": v(-24.48, 13) * mm, "end": v(-14.48, 13) * mm});
            skLineSegment(sketch, "E19.0.1.1", {"start": v(-24.48, 13) * mm, "end": v(-24.48, 3) * mm});
            skLineSegment(sketch, "E19.0.1.2", {"start": v(-14.48, 13) * mm, "end": v(-14.48, 3) * mm});
            skLineSegment(sketch, "E19.0.1.3", {"start": v(-24.48, 3) * mm, "end": v(-14.48, 3) * mm});
            skLineSegment(sketch, "E19.0.2.0", {"start": v(-24.48, -1.5) * mm, "end": v(-14.48, -1.5) * mm});
            skLineSegment(sketch, "E19.0.2.1", {"start": v(-24.48, -1.5) * mm, "end": v(-24.48, -11.5) * mm});
            skLineSegment(sketch, "E19.0.2.2", {"start": v(-14.48, -1.5) * mm, "end": v(-14.48, -11.5) * mm});
            skLineSegment(sketch, "E19.0.2.3", {"start": v(-24.48, -11.5) * mm, "end": v(-14.48, -11.5) * mm});
            skLineSegment(sketch, "E19.0.3.0", {"start": v(-24.48, -16) * mm, "end": v(-14.48, -16) * mm});
            skLineSegment(sketch, "E19.0.3.1", {"start": v(-24.48, -16) * mm, "end": v(-24.48, -26) * mm});
            skLineSegment(sketch, "E19.0.3.2", {"start": v(-14.48, -16) * mm, "end": v(-14.48, -26) * mm});
            skLineSegment(sketch, "E19.0.3.3", {"start": v(-24.48, -26) * mm, "end": v(-14.48, -26) * mm});
            skLineSegment(sketch, "E19.1.0.0", {"start": v(-9.98, 27.5) * mm, "end": v(0.02, 27.5) * mm});
            skLineSegment(sketch, "E19.1.0.1", {"start": v(-9.98, 27.5) * mm, "end": v(-9.98, 17.5) * mm});
            skLineSegment(sketch, "E19.1.0.2", {"start": v(0.02, 27.5) * mm, "end": v(0.02, 17.5) * mm});
            skLineSegment(sketch, "E19.1.0.3", {"start": v(-9.98, 17.5) * mm, "end": v(0.02, 17.5) * mm});
            skLineSegment(sketch, "E19.1.1.0", {"start": v(-9.98, 13) * mm, "end": v(0.02, 13) * mm});
            skLineSegment(sketch, "E19.1.1.1", {"start": v(-9.98, 13) * mm, "end": v(-9.98, 3) * mm});
            skLineSegment(sketch, "E19.1.1.2", {"start": v(0.02, 13) * mm, "end": v(0.02, 3) * mm});
            skLineSegment(sketch, "E19.1.1.3", {"start": v(-9.98, 3) * mm, "end": v(0.02, 3) * mm});
            skLineSegment(sketch, "E19.1.2.0", {"start": v(-9.98, -1.5) * mm, "end": v(0.02, -1.5) * mm});
            skLineSegment(sketch, "E19.1.2.1", {"start": v(-9.98, -1.5) * mm, "end": v(-9.98, -11.5) * mm});
            skLineSegment(sketch, "E19.1.2.2", {"start": v(0.02, -1.5) * mm, "end": v(0.02, -11.5) * mm});
            skLineSegment(sketch, "E19.1.2.3", {"start": v(-9.98, -11.5) * mm, "end": v(0.02, -11.5) * mm});
            skLineSegment(sketch, "E19.1.3.0", {"start": v(-9.98, -16) * mm, "end": v(0.02, -16) * mm});
            skLineSegment(sketch, "E19.1.3.1", {"start": v(-9.98, -16) * mm, "end": v(-9.98, -26) * mm});
            skLineSegment(sketch, "E19.1.3.2", {"start": v(0.02, -16) * mm, "end": v(0.02, -26) * mm});
            skLineSegment(sketch, "E19.1.3.3", {"start": v(-9.98, -26) * mm, "end": v(0.02, -26) * mm});
            skLineSegment(sketch, "E19.2.0.0", {"start": v(4.52, 27.5) * mm, "end": v(14.52, 27.5) * mm});
            skLineSegment(sketch, "E19.2.0.1", {"start": v(4.52, 27.5) * mm, "end": v(4.52, 17.5) * mm});
            skLineSegment(sketch, "E19.2.0.2", {"start": v(14.52, 27.5) * mm, "end": v(14.52, 17.5) * mm});
            skLineSegment(sketch, "E19.2.0.3", {"start": v(4.52, 17.5) * mm, "end": v(14.52, 17.5) * mm});
            skLineSegment(sketch, "E19.2.1.0", {"start": v(4.52, 13) * mm, "end": v(14.52, 13) * mm});
            skLineSegment(sketch, "E19.2.1.1", {"start": v(4.52, 13) * mm, "end": v(4.52, 3) * mm});
            skLineSegment(sketch, "E19.2.1.2", {"start": v(14.52, 13) * mm, "end": v(14.52, 3) * mm});
            skLineSegment(sketch, "E19.2.1.3", {"start": v(4.52, 3) * mm, "end": v(14.52, 3) * mm});
            skLineSegment(sketch, "E19.2.2.0", {"start": v(4.52, -1.5) * mm, "end": v(14.52, -1.5) * mm});
            skLineSegment(sketch, "E19.2.2.1", {"start": v(4.52, -1.5) * mm, "end": v(4.52, -11.5) * mm});
            skLineSegment(sketch, "E19.2.2.2", {"start": v(14.52, -1.5) * mm, "end": v(14.52, -11.5) * mm});
            skLineSegment(sketch, "E19.2.2.3", {"start": v(4.52, -11.5) * mm, "end": v(14.52, -11.5) * mm});
            skLineSegment(sketch, "E19.2.3.0", {"start": v(4.52, -16) * mm, "end": v(14.52, -16) * mm});
            skLineSegment(sketch, "E19.2.3.1", {"start": v(4.52, -16) * mm, "end": v(4.52, -26) * mm});
            skLineSegment(sketch, "E19.2.3.2", {"start": v(14.52, -16) * mm, "end": v(14.52, -26) * mm});
            skLineSegment(sketch, "E19.2.3.3", {"start": v(4.52, -26) * mm, "end": v(14.52, -26) * mm});
            skLineSegment(sketch, "E19.3.0.0", {"start": v(19.02, 27.5) * mm, "end": v(29.02, 27.5) * mm});
            skLineSegment(sketch, "E19.3.0.1", {"start": v(19.02, 27.5) * mm, "end": v(19.02, 17.5) * mm});
            skLineSegment(sketch, "E19.3.0.2", {"start": v(29.02, 27.5) * mm, "end": v(29.02, 17.5) * mm});
            skLineSegment(sketch, "E19.3.0.3", {"start": v(19.02, 17.5) * mm, "end": v(29.02, 17.5) * mm});
            skLineSegment(sketch, "E19.3.1.0", {"start": v(19.02, 13) * mm, "end": v(29.02, 13) * mm});
            skLineSegment(sketch, "E19.3.1.1", {"start": v(19.02, 13) * mm, "end": v(19.02, 3) * mm});
            skLineSegment(sketch, "E19.3.1.2", {"start": v(29.02, 13) * mm, "end": v(29.02, 3) * mm});
            skLineSegment(sketch, "E19.3.1.3", {"start": v(19.02, 3) * mm, "end": v(29.02, 3) * mm});
            skLineSegment(sketch, "E19.3.2.0", {"start": v(19.02, -1.5) * mm, "end": v(29.02, -1.5) * mm});
            skLineSegment(sketch, "E19.3.2.1", {"start": v(19.02, -1.5) * mm, "end": v(19.02, -11.5) * mm});
            skLineSegment(sketch, "E19.3.2.2", {"start": v(29.02, -1.5) * mm, "end": v(29.02, -11.5) * mm});
            skLineSegment(sketch, "E19.3.2.3", {"start": v(19.02, -11.5) * mm, "end": v(29.02, -11.5) * mm});
            skLineSegment(sketch, "E19.3.3.0", {"start": v(19.02, -16) * mm, "end": v(29.02, -16) * mm});
            skLineSegment(sketch, "E19.3.3.1", {"start": v(19.02, -16) * mm, "end": v(19.02, -26) * mm});
            skLineSegment(sketch, "E19.3.3.2", {"start": v(29.02, -16) * mm, "end": v(29.02, -26) * mm});
            skLineSegment(sketch, "E19.3.3.3", {"start": v(19.02, -26) * mm, "end": v(29.02, -26) * mm});
            skLineSegment(sketch, "E19.direction1", {"start": v(-24.48, 27.5) * mm, "end": v(-9.98, 27.5) * mm, "construction": true});
            skLineSegment(sketch, "E19.direction2", {"start": v(-24.48, 27.5) * mm, "end": v(-24.48, 13) * mm, "construction": true});
            skSolve(sketch);
        }
        {
            var Q0;
            Q0 = qSketchRegion(id + "F11", true);
            extrude(context, id + "F12", {"entities" : qUnion([Q0]), "operationType" : NewBodyOperationType.REMOVE, "endBound" : BoundingType.THROUGH_ALL, "oppositeDirection" : true, "depth" : 25 * mm});
        }
    });
